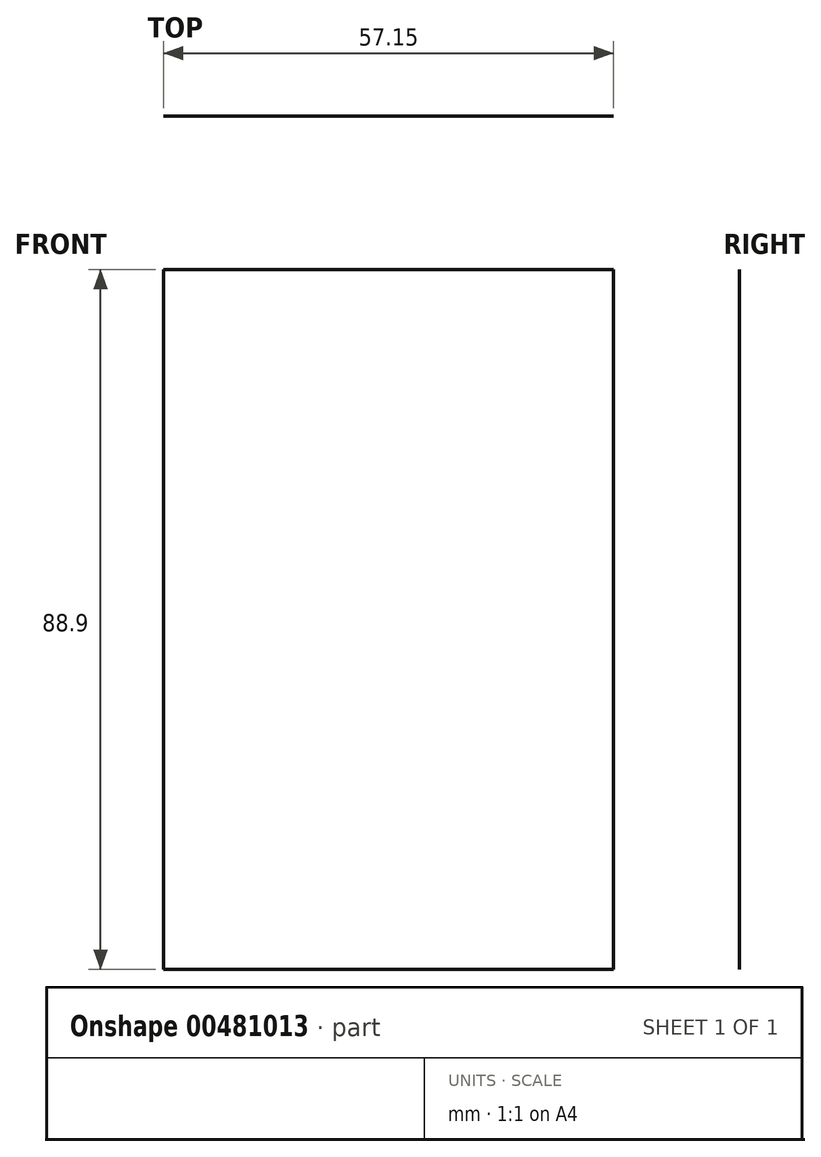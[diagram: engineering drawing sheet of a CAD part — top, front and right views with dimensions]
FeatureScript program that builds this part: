
annotation { "Feature Type Name" : "Feature", "Feature Type Description" : "" }
export const myFeature = defineFeature(function(context is Context, id is Id, definition is map)
    precondition{}
    {
        {
            var Q0;
            Q0=qCreatedBy(makeId("Front.planeOp"),FACE);
            var sketch = newSketch(context, id + "F0", { "sketchPlane" : qUnion([Q0])});
            skLineSegment(sketch, "E0.bottom", {"start": v(-27.25, 44.45) * mm, "end": v(29.9, 44.45) * mm});
            skLineSegment(sketch, "E0.top", {"start": v(-27.25, -44.45) * mm, "end": v(29.9, -44.45) * mm});
            skLineSegment(sketch, "E0.left", {"start": v(-27.25, 44.45) * mm, "end": v(-27.25, -44.45) * mm});
            skLineSegment(sketch, "E0.right", {"start": v(29.9, 44.45) * mm, "end": v(29.9, -44.45) * mm});
            skPoint(sketch, "E0.middle", {"position": v(1.33, 0) * mm});
            skSolve(sketch);
        }
        {
            var Q0;
            Q0=makeQuery(id+"F0.imprint","IMPRINT",FACE,{"disambiguationData":[TD([[makeQuery(id+"F0.imprint","IMPRINT",EDGE,{"derivedFrom":sQuery(id+"F0.wireOp",EDGE,"E0.bottom")}),-1.0]])]});
            extrude(context, id + "F1", {"entities" : qUnion([Q0]), "depth" : 1 / 203.2 * mm});
        }
    });
